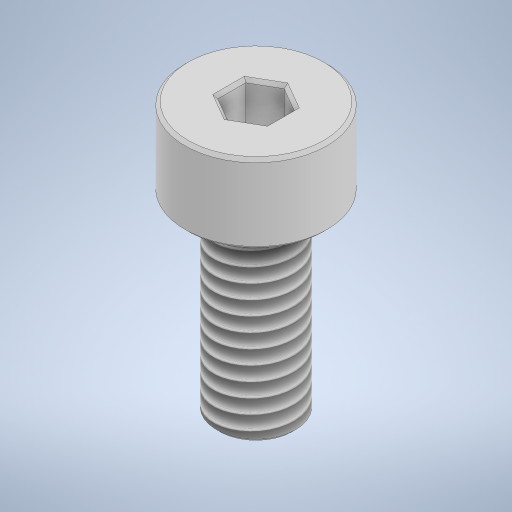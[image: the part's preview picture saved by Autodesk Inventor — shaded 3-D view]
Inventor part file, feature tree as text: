
AUTODESK INVENTOR PART (.ipt)
format: ipt  version: 2023 (Build 270158000, 158)  size: 306,688 bytes
history: native  units: in
note: dims shown in document units (in); Inventor stores cm internally (conversion verified against a paired STEP export)
features: sketch x2, revolve x1, thread x1, extrude x1, chamfer x1
ambient origin geometry x8: Origin, YZ Plane, XZ Plane, XY Plane, X Axis, Y Axis, Z Axis, Center Point
bodies: Solid1 (feature_tree)
feature tree (6):
  revolve  "Revolution1"  [1 undecoded]
  thread  "Thread1"  [1 undecoded]
  extrude  "Extrusion2"  TaperAngle=90.0deg  [1 undecoded]
  chamfer  "Chamfer2"  Distance=0.2362in
  sketch  "Sketch1"  dims[d0=0.0886in d1=0.0984in d2=0.2362in]
  sketch  "Sketch3"  dims[d3=0.0492in d4=90.0deg d5=0.2362in d6=0.0in d13=0.0606in d14=0.0591in d15=0.0in d16=0.0039in d17=0.0787in d18=45.0deg]
note: 3 required parameter values undecoded (feature->parameter linkage not recoverable at this tier; creation-order binding heuristic only, values carry confidence <= 0.55)